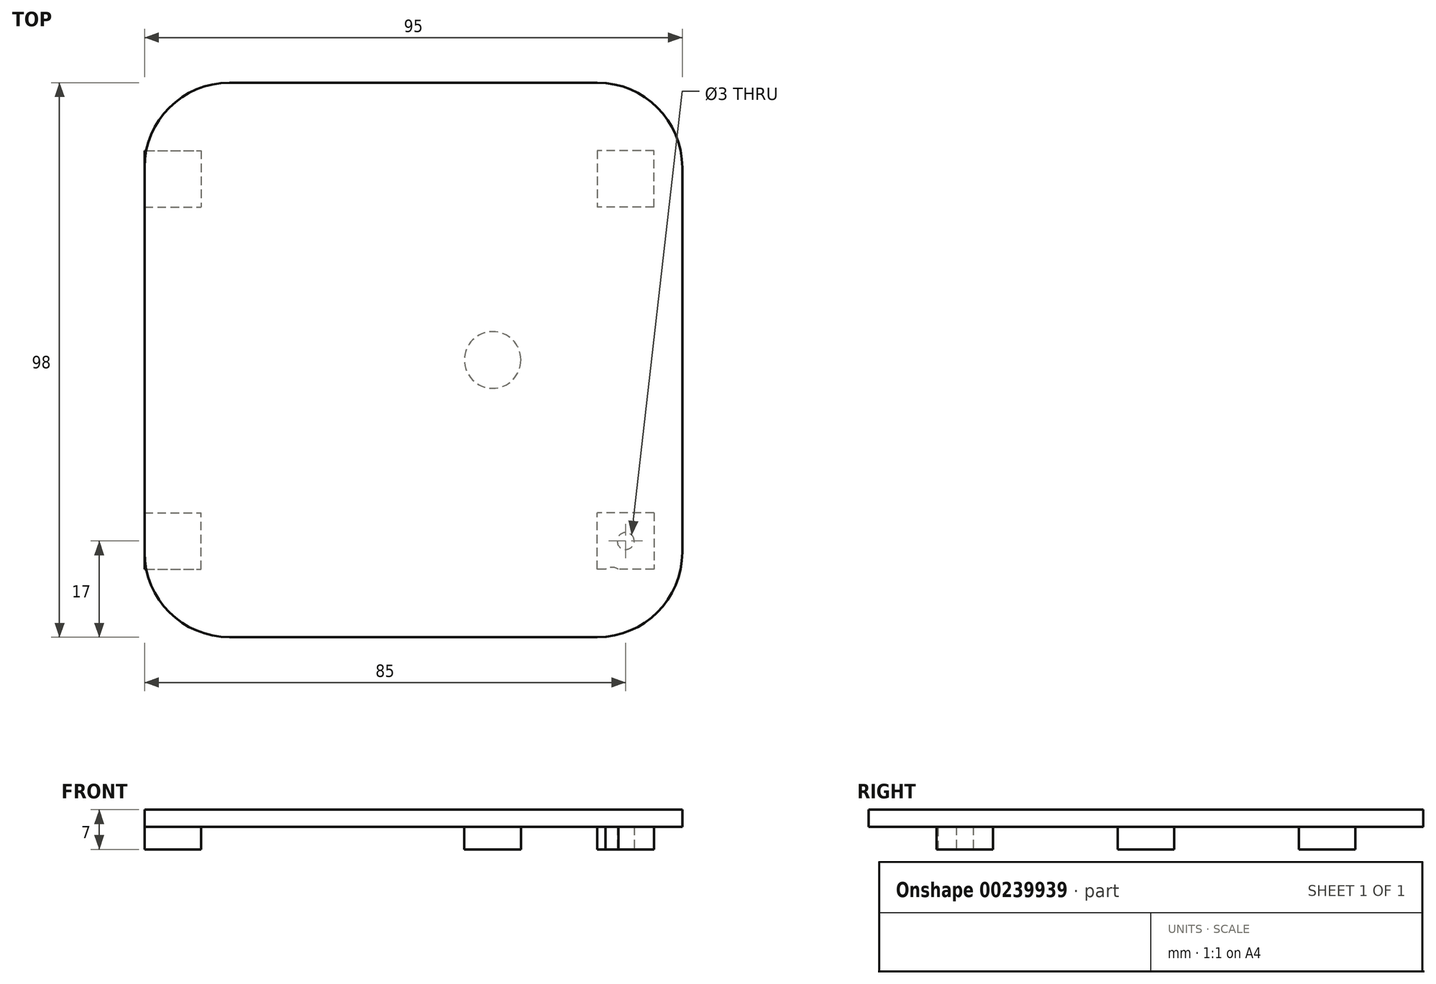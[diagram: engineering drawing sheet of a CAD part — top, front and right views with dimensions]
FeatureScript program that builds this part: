
annotation { "Feature Type Name" : "Feature", "Feature Type Description" : "" }
export const myFeature = defineFeature(function(context is Context, id is Id, definition is map)
    precondition{}
    {
        {
            var Q0;
            Q0=qCreatedBy(makeId("Top.planeOp"),FACE);
            var sketch = newSketch(context, id + "F0", { "sketchPlane" : qUnion([Q0])});
            skLineSegment(sketch, "E0.bottom", {"start": v(50, -49) * mm, "end": v(-45, -49) * mm});
            skLineSegment(sketch, "E0.top", {"start": v(50, 49) * mm, "end": v(-45, 49) * mm});
            skLineSegment(sketch, "E0.left", {"start": v(50, -49) * mm, "end": v(50, 49) * mm});
            skLineSegment(sketch, "E0.right", {"start": v(-45, -49) * mm, "end": v(-45, 49) * mm});
            skPoint(sketch, "E0.middle", {"position": v(2.5, 0) * mm});
            skSolve(sketch);
        }
        {
            var Q0;
            Q0=qCreatedBy(makeId("Top.planeOp"),FACE);
            var sketch = newSketch(context, id + "F1", { "sketchPlane" : qUnion([Q0])});
            skCircle(sketch, "E1", {"center": v(-40, 32) * mm, "radius": 1.5 * mm});
            skCircle(sketch, "E2", {"center": v(40, 32) * mm, "radius": 1.5 * mm});
            skSolve(sketch);
        }
        {
            var Q0;
            Q0=makeQuery(id+"F0.imprint","IMPRINT",FACE,{"disambiguationData":[TD([[makeQuery(id+"F0.imprint","IMPRINT",EDGE,{"derivedFrom":sQuery(id+"F0.wireOp",EDGE,"E0.bottom")}),-1.0]])]});
            extrude(context, id + "F2", {"entities" : qUnion([Q0]), "depth" : 3 * mm});
        }
        {
            var Q0;
            Q0=makeQuery(id+"F1.imprint","IMPRINT",FACE,{"disambiguationData":[TD([[makeQuery(id+"F1.imprint","IMPRINT",EDGE,{"derivedFrom":sQuery(id+"F1.wireOp",EDGE,"E2")}),1.0]])]});
            var Q1;
            Q1=makeQuery(id+"F1.imprint","IMPRINT",FACE,{"disambiguationData":[TD([[makeQuery(id+"F1.imprint","IMPRINT",EDGE,{"derivedFrom":sQuery(id+"F1.wireOp",EDGE,"E1")}),1.0]])]});
            extrude(context, id + "F3", {"entities" : qUnion([Q0, Q1]), "depth" : 25 * mm, "hasSecondDirection" : true, "secondDirectionOppositeDirection" : true, "secondDirectionDepth" : 25 * mm});
        }
        {
            var Q0;
            Q0=makeQuery(id+"F3.opExtrude","SWEPT_BODY",BODY,{"disambiguationData":[OSD([sQuery(id+"F1.wireOp",EDGE,"E1")])]});
            var Q1;
            Q1=makeQuery(id+"F3.opExtrude","SWEPT_BODY",BODY,{"disambiguationData":[OSD([sQuery(id+"F1.wireOp",EDGE,"E2")])]});
            var Q2;
            Q2=qCreatedBy(makeId("Front.planeOp"),FACE);
            mirror(context, id + "F4", {"entities" : qUnion([Q0, Q1]), "mirrorPlane" : qUnion([Q2])});
        }
        {
            var Q0;
            Q0=makeQuery(id+"F2.opExtrude","CAP_FACE",FACE,{"disambiguationData":[OSD([sQuery(id+"F0.wireOp",EDGE,"E0.bottom"),sQuery(id+"F0.wireOp",EDGE,"E0.top"),sQuery(id+"F0.wireOp",EDGE,"E0.left"),sQuery(id+"F0.wireOp",EDGE,"E0.right")])],"isStart":true});
            var sketch = newSketch(context, id + "F5", { "sketchPlane" : qUnion([Q0])});
            skCircle(sketch, "E3", {"center": v(16.5, 0) * mm, "radius": 5 * mm});
            skSolve(sketch);
        }
        {
            var Q0;
            Q0=makeQuery(id+"F5.imprint","IMPRINT",FACE,{"disambiguationData":[TD([[makeQuery(id+"F5.imprint","IMPRINT",EDGE,{"derivedFrom":sQuery(id+"F5.wireOp",EDGE,"E3")}),1.0]])]});
            extrude(context, id + "F6", {"entities" : qUnion([Q0]), "depth" : 4 * mm});
        }
        {
            var Q0;
            {var subQ0=makeQuery(id+"F2yYHvhQEY3OoVR_1.opExtrude","CAP_FACE",FACE,{"disambiguationData":[OSD([sQuery(id+"FPfK7pV33jQlSzm_1.wireOp",EDGE,"AUClnHIZ-HfBY-bZxf-PmzZ-iwxHtC5RBwvf.bottom"),sQuery(id+"FPfK7pV33jQlSzm_1.wireOp",EDGE,"AUClnHIZ-HfBY-bZxf-PmzZ-iwxHtC5RBwvf.top"),sQuery(id+"FPfK7pV33jQlSzm_1.wireOp",EDGE,"AUClnHIZ-HfBY-bZxf-PmzZ-iwxHtC5RBwvf.left"),sQuery(id+"FPfK7pV33jQlSzm_1.wireOp",EDGE,"AUClnHIZ-HfBY-bZxf-PmzZ-iwxHtC5RBwvf.right")])],"isStart":true});var subQ1=makeQuery(id+"FB74mjIpF6BR1jO_2.opPattern","COPY",FACE,{"derivedFrom":subQ0,"instanceName":"1"});Q0=makeQuery(id+"FPYTzfSvbeqYUjv_2.opBoolean","MERGE",FACE,{"derivedFrom":[makeQuery(id+"F2.opExtrude","CAP_FACE",FACE,{"disambiguationData":[OSD([sQuery(id+"F0.wireOp",EDGE,"E0.bottom"),sQuery(id+"F0.wireOp",EDGE,"E0.top"),sQuery(id+"F0.wireOp",EDGE,"E0.left"),sQuery(id+"F0.wireOp",EDGE,"E0.right")])],"isStart":false}),subQ0,subQ1,makeQuery(id+"FZgDihOmzdoeMtR_2.opPattern","COPY",FACE,{"derivedFrom":subQ0,"instanceName":"1"}),makeQuery(id+"FZgDihOmzdoeMtR_2.opPattern","COPY",FACE,{"derivedFrom":subQ1,"instanceName":"1"})]});}
            var sketch = newSketch(context, id + "F7", { "sketchPlane" : qUnion([Q0])});
            skLineSegment(sketch, "E4.bottom", {"start": v(-43.18, 9.6) * mm, "end": v(43.18, 9.6) * mm});
            skLineSegment(sketch, "E4.top", {"start": v(-43.18, -45) * mm, "end": v(43.18, -45) * mm});
            skLineSegment(sketch, "E4.left", {"start": v(-43.18, 9.6) * mm, "end": v(-43.18, -45) * mm});
            skLineSegment(sketch, "E4.right", {"start": v(43.18, 9.6) * mm, "end": v(43.18, -45) * mm});
            skCircle(sketch, "E5", {"center": v(-28.57, 6.57) * mm, "radius": 2 * mm});
            skCircle(sketch, "E6", {"center": v(-28.57, -41.82) * mm, "radius": 2 * mm});
            skCircle(sketch, "E7", {"center": v(37.6, 3.26) * mm, "radius": 2 * mm});
            skCircle(sketch, "E8", {"center": v(37.6, -38.65) * mm, "radius": 2 * mm});
            skLineSegment(sketch, "E9.bottom", {"start": v(-43.18, -5) * mm, "end": v(-35.18, -5) * mm});
            skLineSegment(sketch, "E9.top", {"start": v(-43.18, 2.75) * mm, "end": v(-35.18, 2.75) * mm});
            skLineSegment(sketch, "E9.left", {"start": v(-43.18, -5) * mm, "end": v(-43.18, 2.75) * mm});
            skLineSegment(sketch, "E9.right", {"start": v(-35.18, -5) * mm, "end": v(-35.18, 2.75) * mm});
            skSolve(sketch);
        }
        {
            var Q0;
            Q0=makeQuery(id+"F0.imprint","IMPRINT",FACE,{"disambiguationData":[TD([[makeQuery(id+"F0.imprint","IMPRINT",EDGE,{"derivedFrom":sQuery(id+"F0.wireOp",EDGE,"E0.bottom")}),-1.0]])]});
            var sketch = newSketch(context, id + "F8", { "sketchPlane" : qUnion([Q0])});
            skLineSegment(sketch, "E10.bottom", {"start": v(-45, 37) * mm, "end": v(-35, 37) * mm});
            skLineSegment(sketch, "E10.top", {"start": v(-45, 27) * mm, "end": v(-35, 27) * mm});
            skLineSegment(sketch, "E10.left", {"start": v(-45, 37) * mm, "end": v(-45, 27) * mm});
            skLineSegment(sketch, "E10.right", {"start": v(-35, 37) * mm, "end": v(-35, 27) * mm});
            skPoint(sketch, "E10.middle", {"position": v(-40, 32) * mm});
            skSolve(sketch);
        }
        {
            var Q0;
            Q0=makeQuery(id+"F8.imprint","IMPRINT",FACE,{"disambiguationData":[TD([[makeQuery(id+"F8.imprint","IMPRINT",EDGE,{"derivedFrom":sQuery(id+"F8.wireOp",EDGE,"E10.bottom")}),-1.0]])]});
            extrude(context, id + "F9", {"entities" : qUnion([Q0]), "oppositeDirection" : true, "depth" : 4 * mm});
        }
        {
            var Q0;
            Q0=makeQuery(id+"F9.opExtrude","SWEPT_BODY",BODY,{"disambiguationData":[OSD([sQuery(id+"F8.wireOp",EDGE,"E10.bottom"),sQuery(id+"F8.wireOp",EDGE,"E10.top"),sQuery(id+"F8.wireOp",EDGE,"E10.left"),sQuery(id+"F8.wireOp",EDGE,"E10.right")])]});
            var Q1;
            Q1=qCreatedBy(makeId("Front.planeOp"),FACE);
            mirror(context, id + "F10", {"entities" : qUnion([Q0]), "mirrorPlane" : qUnion([Q1])});
        }
        {
            var Q0;
            Q0=makeQuery(id+"F10.opPattern","COPY",BODY,{"derivedFrom":makeQuery(id+"F9.opExtrude","SWEPT_BODY",BODY,{"disambiguationData":[OSD([sQuery(id+"F8.wireOp",EDGE,"E10.bottom"),sQuery(id+"F8.wireOp",EDGE,"E10.top"),sQuery(id+"F8.wireOp",EDGE,"E10.left"),sQuery(id+"F8.wireOp",EDGE,"E10.right")])]}),"instanceName":"1"});
            var Q1;
            Q1=makeQuery(id+"F9.opExtrude","SWEPT_BODY",BODY,{"disambiguationData":[OSD([sQuery(id+"F8.wireOp",EDGE,"E10.bottom"),sQuery(id+"F8.wireOp",EDGE,"E10.top"),sQuery(id+"F8.wireOp",EDGE,"E10.left"),sQuery(id+"F8.wireOp",EDGE,"E10.right")])]});
            var Q2;
            Q2=qCreatedBy(makeId("Right.planeOp"),FACE);
            mirror(context, id + "F11", {"entities" : qUnion([Q0, Q1]), "mirrorPlane" : qUnion([Q2])});
        }
        {
            var Q0;
            Q0=makeQuery(id+"F4.opPattern","COPY",BODY,{"derivedFrom":makeQuery(id+"F3.opExtrude","SWEPT_BODY",BODY,{"disambiguationData":[OSD([sQuery(id+"F1.wireOp",EDGE,"E2")])]}),"instanceName":"1"});
            var Q1;
            Q1=makeQuery(id+"F3.opExtrude","SWEPT_BODY",BODY,{"disambiguationData":[OSD([sQuery(id+"F1.wireOp",EDGE,"E2")])]});
            var Q2;
            Q2=makeQuery(id+"F3.opExtrude","SWEPT_BODY",BODY,{"disambiguationData":[OSD([sQuery(id+"F1.wireOp",EDGE,"E1")])]});
            var Q3;
            Q3=makeQuery(id+"F4.opPattern","COPY",BODY,{"derivedFrom":makeQuery(id+"F3.opExtrude","SWEPT_BODY",BODY,{"disambiguationData":[OSD([sQuery(id+"F1.wireOp",EDGE,"E1")])]}),"instanceName":"1"});
            var Q4;
            Q4=makeQuery(id+"F11.opPattern","COPY",BODY,{"derivedFrom":makeQuery(id+"F10.opPattern","COPY",BODY,{"derivedFrom":makeQuery(id+"F9.opExtrude","SWEPT_BODY",BODY,{"disambiguationData":[OSD([sQuery(id+"F8.wireOp",EDGE,"E10.bottom"),sQuery(id+"F8.wireOp",EDGE,"E10.top"),sQuery(id+"F8.wireOp",EDGE,"E10.left"),sQuery(id+"F8.wireOp",EDGE,"E10.right")])]}),"instanceName":"1"}),"instanceName":"1"});
            booleanBodies(context, id + "F12", {"operationType" : BooleanOperationType.SUBTRACTION, "tools" : qUnion([Q0, Q1, Q2, Q3]), "targets" : qUnion([Q4])});
        }
        {
            var Q0;
            Q0=makeQuery(id+"F7.imprint","IMPRINT",FACE,{"disambiguationData":[TD([[makeQuery(id+"F7.imprint","IMPRINT",EDGE,{"derivedFrom":sQuery(id+"F7.wireOp",EDGE,"E5")}),1.0]])]});
            var Q1;
            Q1=makeQuery(id+"F7.imprint","IMPRINT",FACE,{"disambiguationData":[TD([[makeQuery(id+"F7.imprint","IMPRINT",EDGE,{"derivedFrom":sQuery(id+"F7.wireOp",EDGE,"E7")}),1.0]])]});
            var Q2;
            Q2=makeQuery(id+"F7.imprint","IMPRINT",FACE,{"disambiguationData":[TD([[makeQuery(id+"F7.imprint","IMPRINT",EDGE,{"derivedFrom":sQuery(id+"F7.wireOp",EDGE,"E6")}),1.0]])]});
            var Q3;
            Q3=makeQuery(id+"F7.imprint","IMPRINT",FACE,{"disambiguationData":[TD([[makeQuery(id+"F7.imprint","IMPRINT",EDGE,{"derivedFrom":sQuery(id+"F7.wireOp",EDGE,"E8")}),1.0]])]});
            extrude(context, id + "F13", {"entities" : qUnion([Q0, Q1, Q2, Q3]), "oppositeDirection" : true, "depth" : 25 * mm});
        }
        {
            var Q0;
            Q0=makeQuery(id+"F13.opExtrude","SWEPT_BODY",BODY,{"disambiguationData":[OSD([sQuery(id+"F7.wireOp",EDGE,"E6")])]});
            var Q1;
            Q1=makeQuery(id+"F13.opExtrude","SWEPT_BODY",BODY,{"disambiguationData":[OSD([sQuery(id+"F7.wireOp",EDGE,"E8")])]});
            var Q2;
            Q2=makeQuery(id+"F13.opExtrude","SWEPT_BODY",BODY,{"disambiguationData":[OSD([sQuery(id+"F7.wireOp",EDGE,"E7")])]});
            var Q3;
            Q3=makeQuery(id+"F13.opExtrude","SWEPT_BODY",BODY,{"disambiguationData":[OSD([sQuery(id+"F7.wireOp",EDGE,"E5")])]});
            var Q4;
            Q4=makeQuery(id+"F11.opPattern","COPY",BODY,{"derivedFrom":makeQuery(id+"F10.opPattern","COPY",BODY,{"derivedFrom":makeQuery(id+"F9.opExtrude","SWEPT_BODY",BODY,{"disambiguationData":[OSD([sQuery(id+"F8.wireOp",EDGE,"E10.bottom"),sQuery(id+"F8.wireOp",EDGE,"E10.top"),sQuery(id+"F8.wireOp",EDGE,"E10.left"),sQuery(id+"F8.wireOp",EDGE,"E10.right")])]}),"instanceName":"1"}),"instanceName":"1"});
            booleanBodies(context, id + "F14", {"operationType" : BooleanOperationType.SUBTRACTION, "tools" : qUnion([Q0, Q1, Q2, Q3]), "targets" : qUnion([Q4])});
        }
        {
            var Q0;
            {var subQ3=sQuery(id+"F7.wireOp",EDGE,"E4.bottom");Q0=makeQuery(id+"F7.imprint","IMPRINT",FACE,{"disambiguationData":[TD([[makeQuery(id+"F7.imprint","IMPRINT",EDGE,{"derivedFrom":subQ3}),1.0]])]});}
            var sketch = newSketch(context, id + "F15", { "sketchPlane" : qUnion([Q0])});
            skLineSegment(sketch, "E11.bottom", {"start": v(-43, 47) * mm, "end": v(7, 47) * mm});
            skLineSegment(sketch, "E11.top", {"start": v(-43, 15) * mm, "end": v(7, 15) * mm});
            skLineSegment(sketch, "E11.left", {"start": v(-43, 47) * mm, "end": v(-43, 15) * mm});
            skLineSegment(sketch, "E11.right", {"start": v(7, 47) * mm, "end": v(7, 15) * mm});
            skCircle(sketch, "E12", {"center": v(-28.44, 27.16) * mm, "radius": 2 * mm});
            skCircle(sketch, "E13", {"center": v(-8.44, 27.16) * mm, "radius": 2 * mm});
            skSolve(sketch);
        }
        {
            var Q0;
            Q0=makeQuery(id+"F15.imprint","IMPRINT",FACE,{"disambiguationData":[TD([[makeQuery(id+"F15.imprint","IMPRINT",EDGE,{"derivedFrom":sQuery(id+"F15.wireOp",EDGE,"E12")}),1.0]])]});
            var Q1;
            Q1=makeQuery(id+"F15.imprint","IMPRINT",FACE,{"disambiguationData":[TD([[makeQuery(id+"F15.imprint","IMPRINT",EDGE,{"derivedFrom":sQuery(id+"F15.wireOp",EDGE,"E13")}),1.0]])]});
            extrude(context, id + "F16", {"entities" : qUnion([Q0, Q1]), "oppositeDirection" : true, "depth" : 25 * mm});
        }
        {
            var Q0;
            Q0=makeQuery(id+"F16.opExtrude","SWEPT_BODY",BODY,{"disambiguationData":[OSD([sQuery(id+"F15.wireOp",EDGE,"E13")])]});
            var Q1;
            Q1=makeQuery(id+"F16.opExtrude","SWEPT_BODY",BODY,{"disambiguationData":[OSD([sQuery(id+"F15.wireOp",EDGE,"E12")])]});
            var Q2;
            Q2=makeQuery(id+"F11.opPattern","COPY",BODY,{"derivedFrom":makeQuery(id+"F10.opPattern","COPY",BODY,{"derivedFrom":makeQuery(id+"F9.opExtrude","SWEPT_BODY",BODY,{"disambiguationData":[OSD([sQuery(id+"F8.wireOp",EDGE,"E10.bottom"),sQuery(id+"F8.wireOp",EDGE,"E10.top"),sQuery(id+"F8.wireOp",EDGE,"E10.left"),sQuery(id+"F8.wireOp",EDGE,"E10.right")])]}),"instanceName":"1"}),"instanceName":"1"});
            booleanBodies(context, id + "F17", {"operationType" : BooleanOperationType.SUBTRACTION, "tools" : qUnion([Q0, Q1]), "targets" : qUnion([Q2])});
        }
        {
            var Q0;
            Q0=makeQuery(id+"F2.opExtrude","SWEPT_EDGE",EDGE,{"disambiguationData":[OSD([sQuery(id+"F0.wireOp",EDGE,"E0.bottom"),sQuery(id+"F0.wireOp",EDGE,"E0.right")])]});
            var Q1;
            Q1=makeQuery(id+"F2.opExtrude","SWEPT_EDGE",EDGE,{"disambiguationData":[OSD([sQuery(id+"F0.wireOp",EDGE,"E0.bottom"),sQuery(id+"F0.wireOp",EDGE,"E0.left")])]});
            var Q2;
            Q2=makeQuery(id+"F2.opExtrude","SWEPT_EDGE",EDGE,{"disambiguationData":[OSD([sQuery(id+"F0.wireOp",EDGE,"E0.top"),sQuery(id+"F0.wireOp",EDGE,"E0.left")])]});
            var Q3;
            Q3=makeQuery(id+"F2.opExtrude","SWEPT_EDGE",EDGE,{"disambiguationData":[OSD([sQuery(id+"F0.wireOp",EDGE,"E0.top"),sQuery(id+"F0.wireOp",EDGE,"E0.right")])]});
            fillet(context, id + "F18", {"entities" : qUnion([Q0, Q1, Q2, Q3]), "radius" : 15 * mm, "tangentPropagation" : true, "allowEdgeOverflow" : false});
        }
    });
